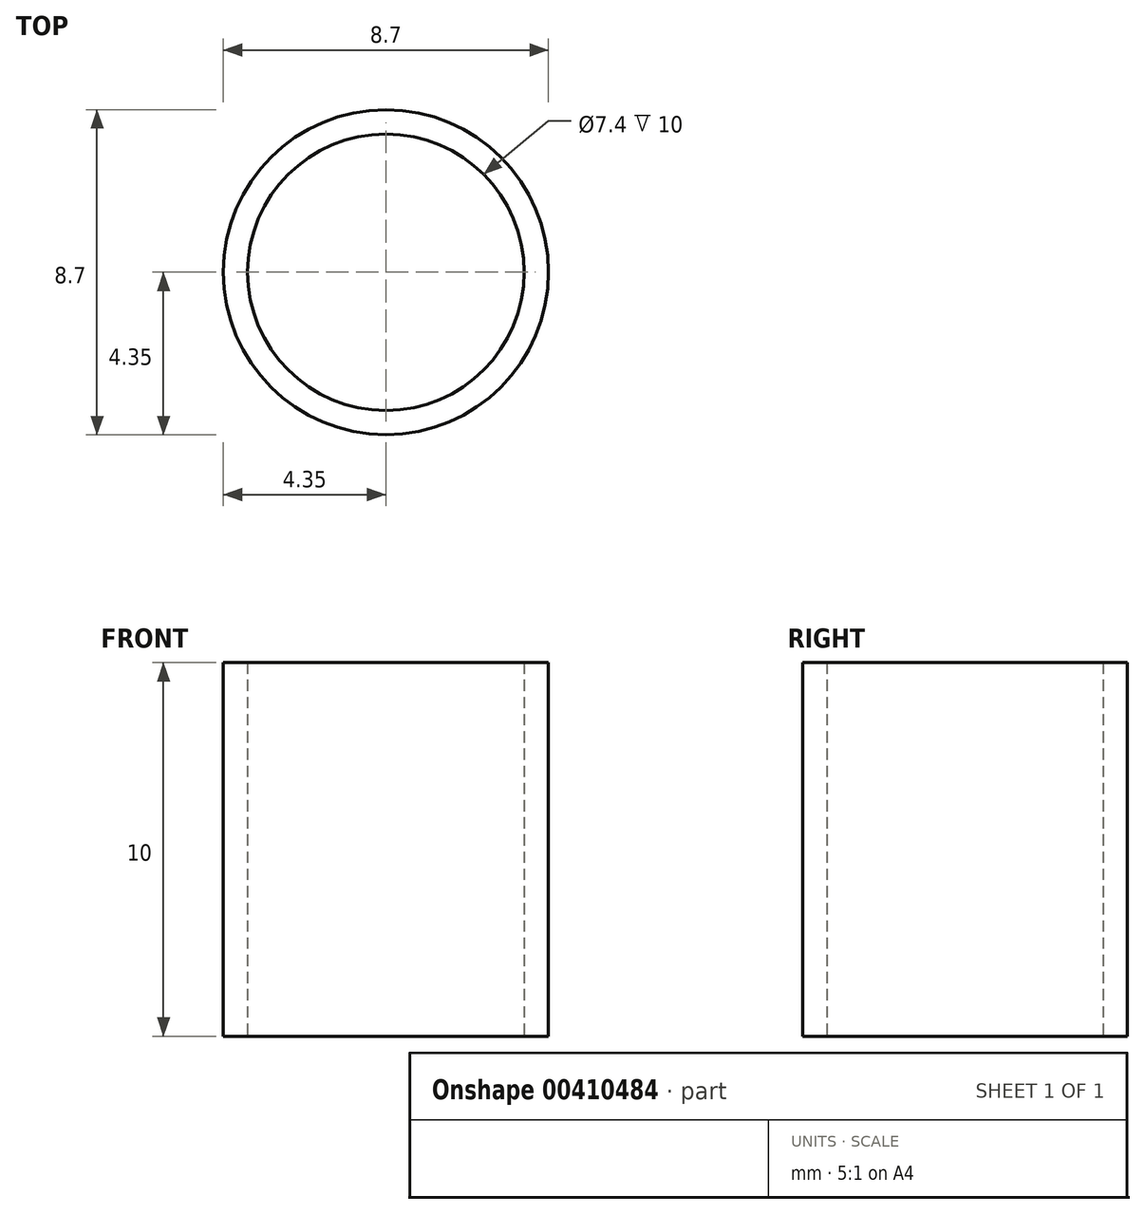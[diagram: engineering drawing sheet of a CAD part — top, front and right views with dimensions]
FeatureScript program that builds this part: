
annotation { "Feature Type Name" : "Feature", "Feature Type Description" : "" }
export const myFeature = defineFeature(function(context is Context, id is Id, definition is map)
    precondition{}
    {
        {
            var Q0;
            Q0=qCreatedBy(makeId("Top.planeOp"),FACE);
            var sketch = newSketch(context, id + "F0", { "sketchPlane" : qUnion([Q0])});
            skCircle(sketch, "E0", {"center": v(0, 0) * mm, "radius": 3.7 * mm});
            skCircle(sketch, "E1", {"center": v(0, 0) * mm, "radius": 4.35 * mm});
            skSolve(sketch);
        }
        {
            var Q0;
            Q0 = qSketchRegion(id + "F0", true);
            extrude(context, id + "F1", {"entities" : qUnion([Q0]), "depth" : 10 * mm, "offsetDistance" : 25 * mm});
        }
    });
